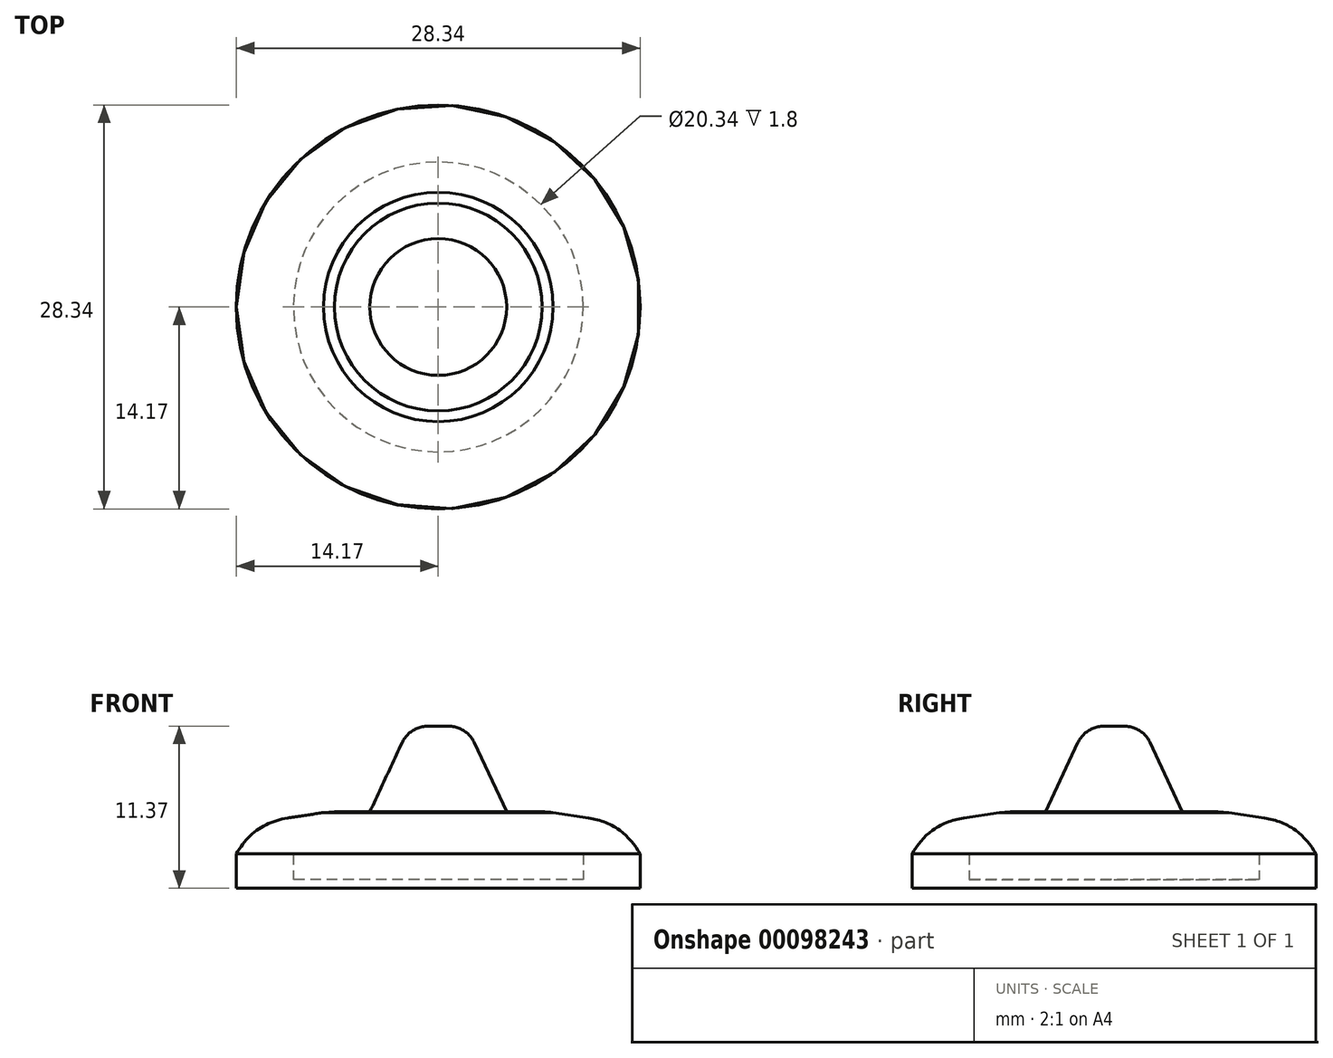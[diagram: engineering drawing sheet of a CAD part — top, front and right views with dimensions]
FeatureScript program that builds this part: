
annotation { "Feature Type Name" : "Feature", "Feature Type Description" : "" }
export const myFeature = defineFeature(function(context is Context, id is Id, definition is map)
    precondition{}
    {
        {
            var Q0;
            Q0=qCreatedBy(makeId("Top.planeOp"),FACE);
            var sketch = newSketch(context, id + "F0", { "sketchPlane" : qUnion([Q0])});
            skCircle(sketch, "E0", {"center": v(0, 0) * mm, "radius": 10.17 * mm});
            skLineSegment(sketch, "E1", {"start": v(36.05, 0) * mm, "end": v(-31.53, 0) * mm, "construction": true});
            skLineSegment(sketch, "E2", {"start": v(0, 15.16) * mm, "end": v(0, -23.8) * mm, "construction": true});
            skSolve(sketch);
        }
        {
            var Q0;
            Q0 = qSketchRegion(id + "F0", true);
            extrude(context, id + "F1", {"entities" : qUnion([Q0]), "depth" : 1.8 * mm});
        }
        {
            var Q0;
            Q0=makeQuery(id+"F1.opExtrude","CAP_FACE",FACE,{"disambiguationData":[OSD([sQuery(id+"F0.wireOp",EDGE,"E0")])],"isStart":false});
            var sketch = newSketch(context, id + "F2", { "sketchPlane" : qUnion([Q0])});
            skCircle(sketch, "E3.0", {"center": v(0, 0) * mm, "radius": 14.17 * mm});
            skPoint(sketch, "E4.start.orphan", {"position": v(-2.12, 0) * mm});
            skPoint(sketch, "E5.orphan", {"position": v(14.17, 0) * mm});
            skSolve(sketch);
        }
        {
            var Q0;
            Q0=makeQuery(id+"F2.imprint","IMPRINT",FACE,{"disambiguationData":[TD([[makeQuery(id+"F2.imprint","IMPRINT",EDGE,{"derivedFrom":sQuery(id+"F2.wireOp",EDGE,"E3.0")}),1.0]])]});
            var Q1;
            Q1=makeQuery(id+"F2.imprint","IMPRINT",FACE,{"disambiguationData":[TD([[makeQuery(id+"F2.imprint","IMPRINT",EDGE,{"derivedFrom":makeQuery(id+"F1.opExtrude","CAP_EDGE",EDGE,{"disambiguationData":[OSD([sQuery(id+"F0.wireOp",EDGE,"E0")])],"isStart":false})}),1.0]])]});
            extrude(context, id + "F3", {"entities" : qUnion([Q0, Q1]), "oppositeDirection" : true, "depth" : 2.4 * mm});
        }
        {
            var Q0;
            Q0=makeQuery(id+"F1.opExtrude","SWEPT_BODY",BODY,{"disambiguationData":[OSD([sQuery(id+"F0.wireOp",EDGE,"E0")])]});
            var Q1;
            Q1=makeQuery(id+"F3.opExtrude","SWEPT_BODY",BODY,{"disambiguationData":[OSD([sQuery(id+"F2.wireOp",EDGE,"E3.0")])]});
            booleanBodies(context, id + "F4", {"operationType" : BooleanOperationType.SUBTRACTION, "tools" : qUnion([Q0]), "targets" : qUnion([Q1]), "keepTools" : true});
        }
        {
            var Q0;
            Q0=qCreatedBy(makeId("Right.planeOp"),FACE);
            var sketch = newSketch(context, id + "F5", { "sketchPlane" : qUnion([Q0])});
            skLineSegment(sketch, "E6.0", {"start": v(-14.17, 1.8) * mm, "end": v(14.17, 1.8) * mm});
            skLineSegment(sketch, "E7", {"start": v(-14.17, 1.8) * mm, "end": v(-14.17, 3.77) * mm});
            skLineSegment(sketch, "E8", {"start": v(-14.17, 3.77) * mm, "end": v(-7.67, 4.77) * mm});
            skLineSegment(sketch, "E9", {"start": v(-7.67, 4.77) * mm, "end": v(-4.8, 4.77) * mm});
            skLineSegment(sketch, "E10", {"start": v(-4.8, 4.77) * mm, "end": v(-2, 10.77) * mm});
            skLineSegment(sketch, "E11", {"start": v(-2, 10.77) * mm, "end": v(0, 10.77) * mm});
            skLineSegment(sketch, "E12", {"start": v(0, 10.77) * mm, "end": v(0, 1.8) * mm});
            skLineSegment(sketch, "E13", {"start": v(0, 1.8) * mm, "end": v(-14.17, 1.8) * mm});
            skSolve(sketch);
        }
        {
            var Q0;
            Q0 = qSketchRegion(id + "F5", true);
            var Q1;
            Q1=sQuery(id+"F2.wireOp",EDGE,"E3.0");
            revolve(context, id + "F6", {"entities" : qUnion([Q0]), "axis" : qUnion([Q1]), "revolveType" : RevolveType.FULL});
        }
        {
            var Q0;
            Q0=makeQuery(id+"F6.opRevolve","SWEPT_EDGE",EDGE,{"disambiguationData":[OSD([sQuery(id+"F5.wireOp",EDGE,"E8"),sQuery(id+"F5.wireOp",EDGE,"E9")])]});
            chamfer(context, id + "F7", {"entities" : qUnion([Q0]), "width" : 5 * mm, "tangentPropagation" : true});
        }
        {
            var Q0;
            Q0=makeQuery(id+"F6.opRevolve","SWEPT_EDGE",EDGE,{"disambiguationData":[OSD([sQuery(id+"F5.wireOp",EDGE,"E10"),sQuery(id+"F5.wireOp",EDGE,"E11")])]});
            fillet(context, id + "F8", {"entities" : qUnion([Q0]), "radius" : 2 * mm, "allowEdgeOverflow" : false});
        }
        {
            var Q0;
            Q0=makeQuery(id+"F6.opRevolve","SWEPT_EDGE",EDGE,{"disambiguationData":[OSD([sQuery(id+"F5.wireOp",EDGE,"E7"),sQuery(id+"F5.wireOp",EDGE,"E8")])]});
            fillet(context, id + "F9", {"entities" : qUnion([Q0]), "radius" : 5 * mm, "tangentPropagation" : true, "rho" : 0.5, "crossSection" : FilletCrossSection.CONIC, "allowEdgeOverflow" : false});
        }
    });
